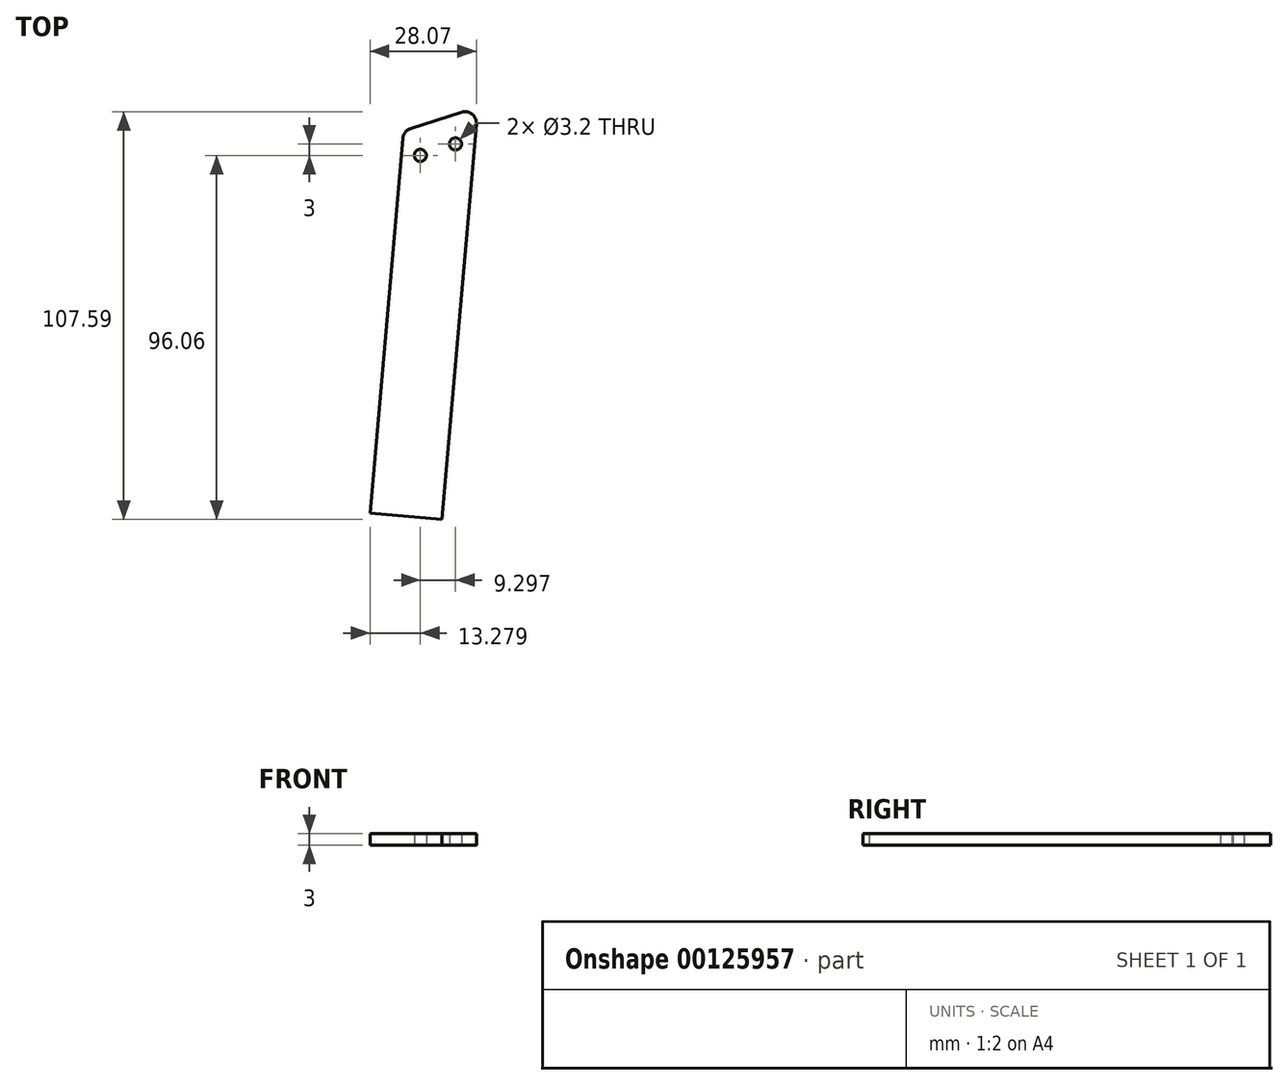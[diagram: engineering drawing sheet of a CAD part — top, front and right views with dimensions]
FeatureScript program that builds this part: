
annotation { "Feature Type Name" : "Feature", "Feature Type Description" : "" }
export const myFeature = defineFeature(function(context is Context, id is Id, definition is map)
    precondition{}
    {
        {
            var Q0;
            Q0=qCreatedBy(makeId("Top.planeOp"),FACE);
            var sketch = newSketch(context, id + "F0", { "sketchPlane" : qUnion([Q0])});
            skLineSegment(sketch, "E0", {"start": v(-19.47, -4.56) * mm, "end": v(-28.12, -103.4) * mm});
            skLineSegment(sketch, "E1", {"start": v(-28.12, -103.4) * mm, "end": v(-9.2, -105.06) * mm});
            skLineSegment(sketch, "E2", {"start": v(-9.2, -105.06) * mm, "end": v(-0.48, -5.44) * mm});
            skCircle(sketch, "E3", {"center": v(-14.84, -9) * mm, "radius": 1.6 * mm});
            skCircle(sketch, "E4", {"center": v(-5.54, -6) * mm, "radius": 1.6 * mm});
            skLineSegment(sketch, "E5", {"start": v(-20.47, -16) * mm, "end": v(-1.4, -16) * mm, "construction": true});
            skLineSegment(sketch, "E6", {"start": v(-14.84, -9) * mm, "end": v(-5.54, -6) * mm, "construction": true});
            skLineSegment(sketch, "E7", {"start": v(-19.47, -4.56) * mm, "end": v(-19.47, -4.54) * mm});
            skLineSegment(sketch, "E8", {"start": v(-17.4, -1.95) * mm, "end": v(-3.97, 2.39) * mm});
            skLineSegment(sketch, "E9", {"start": v(-0.48, -5.44) * mm, "end": v(-0.06, -0.73) * mm});
            skPoint(sketch, "E10.visualSharp", {"position": v(-19.3, -2.56) * mm});
            skArc(sketch, "E10.filletArc", {"start": v(-17.4, -1.95) * mm, "mid": v(-18.83, -2.93) * mm, "end": v(-19.47, -4.54) * mm});
            skPoint(sketch, "E11.visualSharp", {"position": v(0.33, 3.78) * mm});
            skArc(sketch, "E11.filletArc", {"start": v(-0.06, -0.73) * mm, "mid": v(-1.18, 1.88) * mm, "end": v(-3.97, 2.39) * mm});
            skSolve(sketch);
        }
        {
            var Q0;
            Q0=makeQuery(id+"F0.imprint","IMPRINT",FACE,{"disambiguationData":[TD([[makeQuery(id+"F0.imprint","IMPRINT",EDGE,{"derivedFrom":sQuery(id+"F0.wireOp",EDGE,"E0")}),1.0]])]});
            extrude(context, id + "F1", {"entities" : qUnion([Q0]), "depth" : 3 * mm});
        }
    });
